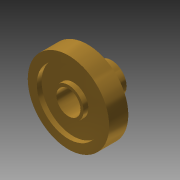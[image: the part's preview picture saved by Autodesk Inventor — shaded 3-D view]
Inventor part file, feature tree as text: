
AUTODESK INVENTOR PART (.ipt)
format: ipt  version: 2015 SP1 (Build 190203100, 203)  size: 128,000 bytes
history: native  units: mm
features: extrude x6, sketch x4, projected_geometry x1
ambient origin geometry x8: Origin, YZ Plane, XZ Plane, XY Plane, X Axis, Y Axis, Z Axis, Center Point
bodies: Solid1 (feature_tree)
feature tree (11):
  sketch  "Sketch1"  dims[d0=10.0mm d1=21.0mm]
  extrude  "Extrusion1"  Depth=10.0mm
  extrude  "Extrusion2"  Depth=6.35mm TaperAngle=0.0deg
  extrude  "Extrusion3"  Depth=6.35mm TaperAngle=0.0deg
  extrude  "Extrusion4"  Depth=8.0mm
  extrude  "Extrusion5"  Depth=7.9375mm TaperAngle=0.0deg
  extrude  "Extrusion6"  Depth=3.175mm
  sketch  "Sketch2"  dims[d2=27.0mm d3=6.35mm d4=0.0mm]
  projected_geometry  "Projected Loop1"
  sketch  "Sketch3"  dims[d5=3.175mm d6=0.0mm d7=6.35mm d8=0.0mm]
  sketch  "Sketch4"  dims[d9=7.9375mm d10=0.0mm d11=8.0mm d12=7.9375mm d13=0.0mm d14=3.175mm d15=7.9375mm d16=0.0mm]
